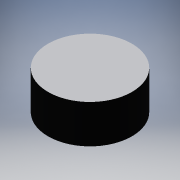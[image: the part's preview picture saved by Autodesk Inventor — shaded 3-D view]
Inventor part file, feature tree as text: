
AUTODESK INVENTOR PART (.ipt)
format: ipt  version: 2016 (Build 200138000, 138)  size: 200,192 bytes
history: native  units: in
note: dims shown in document units (in); Inventor stores cm internally (conversion verified against a paired STEP export)
features: thread x8, sketch x6, extrude x4, hole x2, plane x2, chamfer x1, revolve x1, split x1
ambient origin geometry x8: Origin, YZ Plane, XZ Plane, XY Plane, X Axis, Y Axis, Z Axis, Center Point
bodies: Solid1 (feature_tree)
feature tree (25):
  extrude  "Extrusion1"  Depth=1.5157in TaperAngle=0.0deg
  extrude  "Extrusion2"  Depth=0.9213in TaperAngle=0.0deg
  chamfer  "Chamfer1"  Distance=0.1181in Angle=45.0deg
  sketch  "Sketch3"  dims[d10=0.4134in d14=0.2264in d15=0.2264in d16=1.1811in d17=1.1811in]
  hole  "Hole1"  [1 undecoded]
  thread  "Thread1"  [1 undecoded]
  thread  "Thread2"  [1 undecoded]
  thread  "Thread3"  [1 undecoded]
  thread  "Thread4"  [1 undecoded]
  extrude  "Extrusion3"  Depth=0.3937in TaperAngle=0.0deg
  hole  "Hole2"  [1 undecoded]
  thread  "Thread5"  [1 undecoded]
  thread  "Thread6"  [1 undecoded]
  thread  "Thread7"  [1 undecoded]
  thread  "Thread8"  [1 undecoded]
  plane  "Work Plane1"
  sketch  "Sketch4"  dims[d18=0.0984in d19=0.2362in d20=0.1575in d21=0.0787in d22=90.0deg d23=0.1575in d24=0.0in d25=0.3937in d26=0.0in]
  extrude  "Extrusion5"  Depth=0.3937in TaperAngle=0.0deg
  revolve  "Revolution1"  [1 undecoded]
  plane  "Work Plane2"
  split  "Split1"
  sketch  "Sketch6"  dims[d31=0.3937in d32=0.0in d33=0.4724in d34=0.0in d35=0.4449in d36=0.4449in d37=0.0827in d38=0.2362in d39=0.1575in d40=0.0787in d41=90.0deg d42=0.1181in d43=0.8108in d44=0.3937in d45=0.0in d46=0.3937in d47=0.0in d48=0.3937in d49=0.0in d50=0.3937in d51=0.0in d52=1.6339in d53=0.0394in d54=0.7874in d55=0.7087in d56=0.5906in d57=0.5906in d58=0.5in d59=0.5in d62=0.5906in d63=0.0in d64=0.0591in d67=0.0394in d68=0.0394in d69=90.0deg d70=0.0in]
  sketch  "Sketch1"  dims[d0=2.5591in d1=1.5157in d2=0.0in]
  sketch  "Sketch2"  dims[d3=2.0079in d4=0.9213in d5=0.0in d7=0.1181in d8=0.0787in d9=45.0deg]
  sketch  "Sketch5"  dims[d27=0.3937in d28=0.0in d29=0.3937in d30=0.0in]
note: 11 required parameter values undecoded (feature->parameter linkage not recoverable at this tier; creation-order binding heuristic only, values carry confidence <= 0.55)